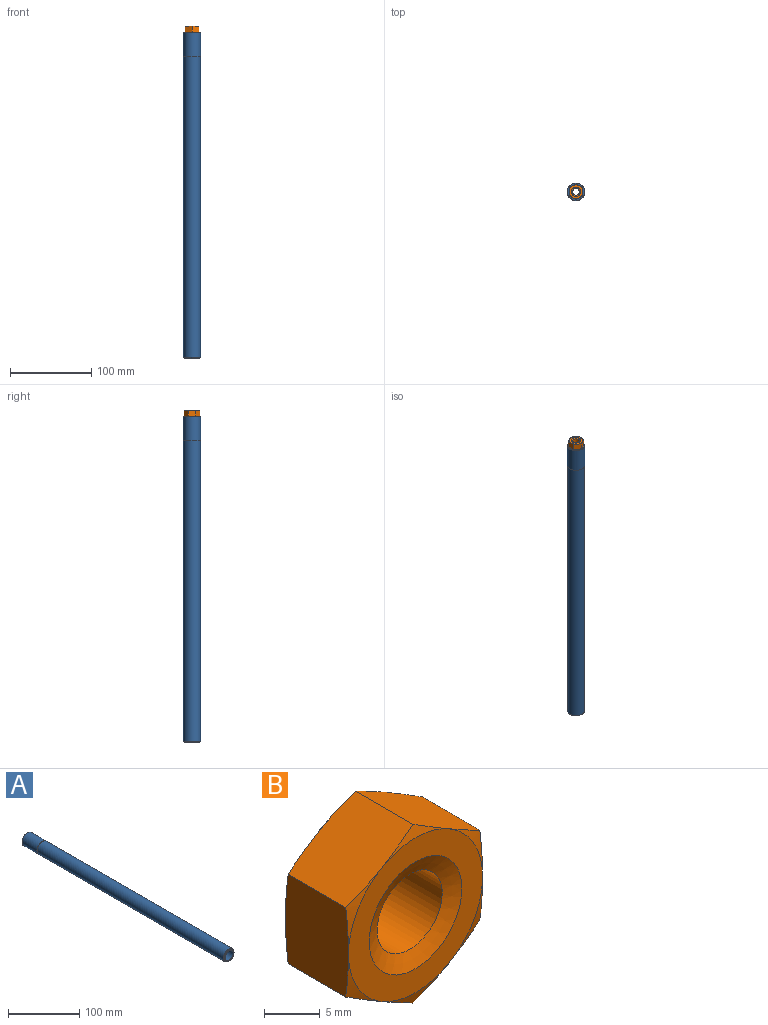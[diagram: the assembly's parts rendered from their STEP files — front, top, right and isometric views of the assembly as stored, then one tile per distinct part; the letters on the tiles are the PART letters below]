
ASSEMBLY  parts=2 mates=1
PART A: 7 faces, bbox 21.3x400x21.3 mm
  f0: cylinder r=10.65mm len=29.7mm, axis (0,-1,0), area 1987.4mm2, adj f2,f6
  f1: cylinder r=8.05mm len=400mm, axis (0,-1,0), area 20231.9mm2, adj f2,f3
  f2: plane 21.3x21.3mm, normal (0,1,0), area 152.7mm2, adj f0,f1
  f3: plane 19.15x19.15mm, normal (0,-1,0), area 84.4mm2, adj f1,f5
  f4: cylinder r=10.48mm len=368.97mm, axis (0,1,0), area 24295.5mm2, adj f5,f6
  f5: cone r=9.57mm half-angle=37.8deg, axis (0,1,0), area 92.9mm2, adj f3,f4
  f6: cone r=10.65mm half-angle=45deg, axis (0,1,0), area 16mm2, adj f0,f4
PART B: 23 faces, bbox 20.4x8.7x20.4 mm
  f0: plane 17x17mm, normal (0,1,0), area 118.5mm2, adj f3,f4,f7,f9,f11,f13,f22
  f1: cylinder r=4.12mm len=8.25mm, axis (0,-1,0), area 168.5mm2, adj f21,f22
  f2: plane 17x17mm, normal (0,-1,0), area 118.5mm2, adj f5,f6,f8,f10,f12,f14,f21
  f3: cone r=9.81mm half-angle=75deg, axis (0,-1,0), area 6.4mm2, adj f0,f15,f20
  f4: cone r=9.81mm half-angle=75deg, axis (0,-1,0), area 6.4mm2, adj f0,f15,f16
  f5: cone r=9.81mm half-angle=75deg, axis (0,1,0), area 6.4mm2, adj f2,f15,f20
  f6: cone r=9.81mm half-angle=75deg, axis (0,1,0), area 6.4mm2, adj f2,f15,f16
  f7: cone r=9.81mm half-angle=75deg, axis (0,-1,0), area 6.4mm2, adj f0,f16,f17
  f8: cone r=9.81mm half-angle=75deg, axis (0,1,0), area 6.4mm2, adj f2,f16,f17
  f9: cone r=9.81mm half-angle=75deg, axis (0,-1,0), area 6.4mm2, adj f0,f17,f18
  f10: cone r=9.81mm half-angle=75deg, axis (0,1,0), area 6.4mm2, adj f2,f17,f18
  f11: cone r=9.81mm half-angle=75deg, axis (0,-1,0), area 6.4mm2, adj f0,f18,f19
  f12: cone r=9.81mm half-angle=75deg, axis (0,1,0), area 6.4mm2, adj f2,f18,f19
  f13: cone r=9.81mm half-angle=75deg, axis (0,-1,0), area 6.4mm2, adj f0,f19,f20
  f14: cone r=9.81mm half-angle=75deg, axis (0,1,0), area 6.4mm2, adj f2,f19,f20
  f15: plane 10.55x8.73mm, normal (-1,0,0), area 76.1mm2, adj f3,f4,f5,f6,f16,f20
  f16: plane 9.23x8.73mm, normal (-0.5,0,0.87), area 76.1mm2, adj f4,f6,f7,f8,f15,f17
  f17: plane 9.23x8.73mm, normal (0.5,0,0.87), area 76.1mm2, adj f7,f8,f9,f10,f16,f18
  f18: plane 10.55x8.73mm, normal (1,0,0), area 76.1mm2, adj f9,f10,f11,f12,f17,f19
  f19: plane 9.23x8.73mm, normal (0.5,0,-0.87), area 76.1mm2, adj f11,f12,f13,f14,f18,f20
  f20: plane 9.23x8.73mm, normal (-0.5,0,-0.87), area 76.1mm2, adj f3,f5,f13,f14,f15,f19
  f21: cone r=5.88mm half-angle=66.8deg, axis (0,-1,0), area 59.8mm2, adj f1,f2
  f22: cone r=4.12mm half-angle=66.8deg, axis (0,1,0), area 59.8mm2, adj f0,f1
PLACE A rot(axis=(1,0,0),90deg) t=(0,0,14.35)mm
PLACE B rot(axis=(1,0,0),90deg) t=(0,0,218.35)mm
MATE fastened B.f22 <-> A.f0  axis (0,0,-1) through (0,0,214.35)mm
